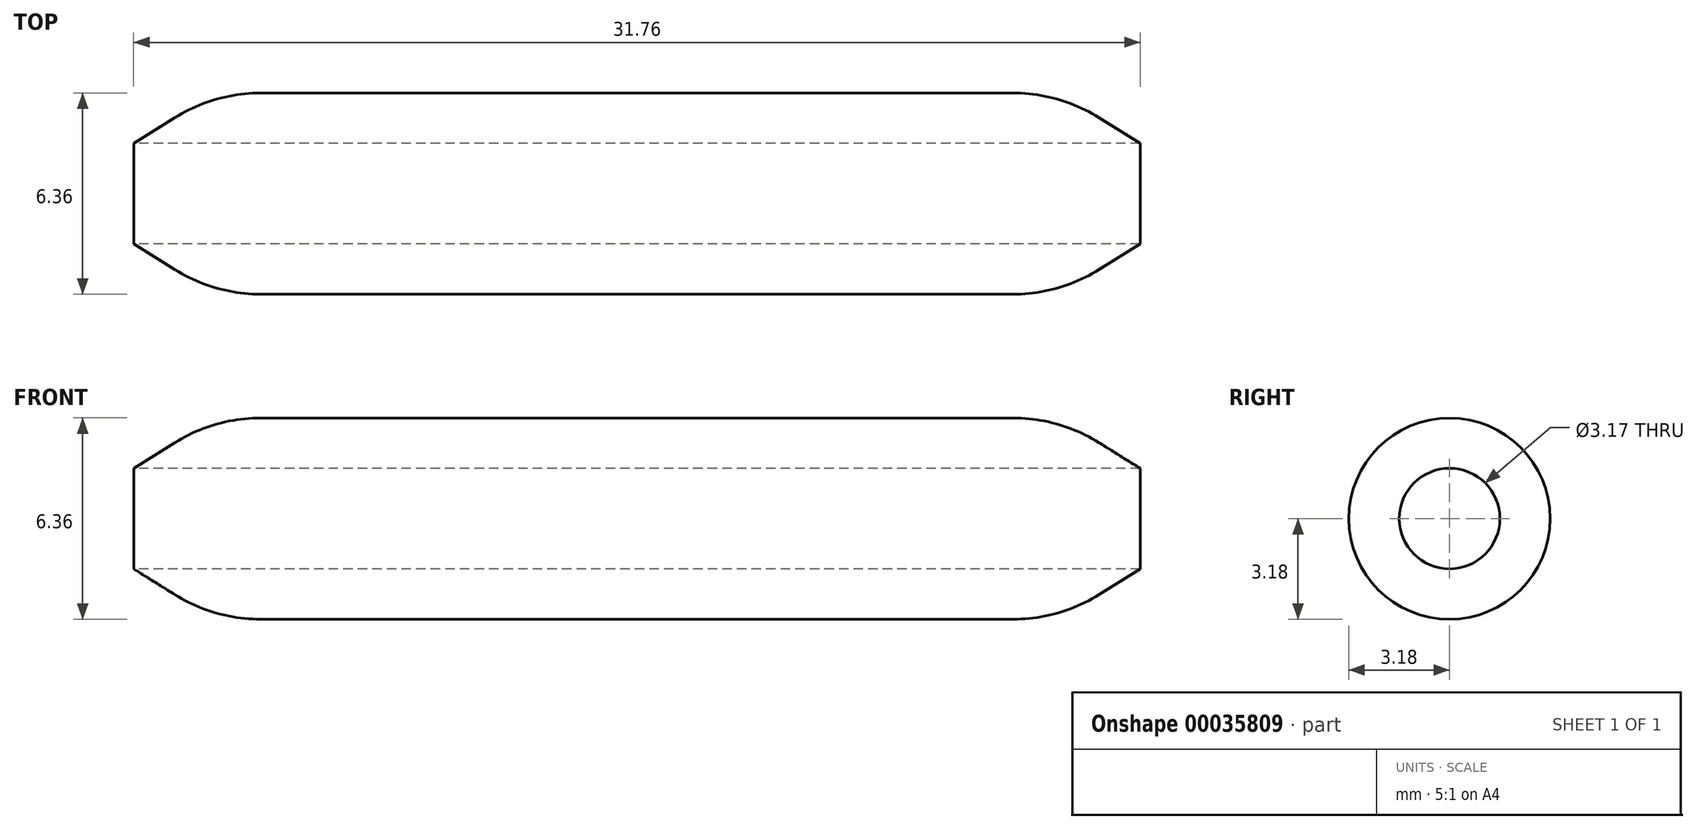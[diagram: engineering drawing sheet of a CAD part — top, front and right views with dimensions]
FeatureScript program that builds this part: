
annotation { "Feature Type Name" : "Feature", "Feature Type Description" : "" }
export const myFeature = defineFeature(function(context is Context, id is Id, definition is map)
    precondition{}
    {
        {
            var Q0;
            Q0=qCreatedBy(makeId("Front.planeOp"),FACE);
            var sketch = newSketch(context, id + "F0", { "sketchPlane" : qUnion([Q0])});
            skLineSegment(sketch, "E0", {"start": v(0, 1.59) * mm, "end": v(-15.88, 1.59) * mm});
            skLineSegment(sketch, "E1", {"start": v(-15.88, 1.59) * mm, "end": v(-13.33, 3.17) * mm});
            skLineSegment(sketch, "E2", {"start": v(-13.33, 3.17) * mm, "end": v(0, 3.17) * mm});
            skLineSegment(sketch, "E3", {"start": v(0, 3.17) * mm, "end": v(0, 1.59) * mm, "construction": true});
            skLineSegment(sketch, "E4.MirrorCS", {"start": v(0, 1.59) * mm, "end": v(15.88, 1.59) * mm});
            skLineSegment(sketch, "E5.MirrorCS", {"start": v(15.88, 1.59) * mm, "end": v(13.33, 3.18) * mm});
            skLineSegment(sketch, "E6.MirrorCS", {"start": v(13.33, 3.18) * mm, "end": v(0, 3.17) * mm});
            skLineSegment(sketch, "E7", {"start": v(-17.51, 0) * mm, "end": v(18.75, 0) * mm});
            skSolve(sketch);
        }
        {
            var Q0;
            Q0 = qSketchRegion(id + "F0", true);
            var Q1;
            Q1=sQuery(id+"F0.wireOp",EDGE,"E7");
            revolve(context, id + "F1", {"entities" : qUnion([Q0]), "axis" : qUnion([Q1]), "revolveType" : RevolveType.FULL});
        }
        {
            var Q0;
            Q0=makeQuery(id+"F1.opRevolve","SWEPT_EDGE",EDGE,{"disambiguationData":[OSD([sQuery(id+"F0.wireOp",EDGE,"E1"),sQuery(id+"F0.wireOp",EDGE,"E2")])]});
            var Q1;
            Q1=makeQuery(id+"F1.opRevolve","SWEPT_EDGE",EDGE,{"disambiguationData":[OSD([sQuery(id+"F0.wireOp",EDGE,"E5.MirrorCS"),sQuery(id+"F0.wireOp",EDGE,"E6.MirrorCS")])]});
            fillet(context, id + "F2", {"entities" : qUnion([Q0, Q1]), "radius" : 5.08 * mm, "tangentPropagation" : true, "allowEdgeOverflow" : false});
        }
    });
